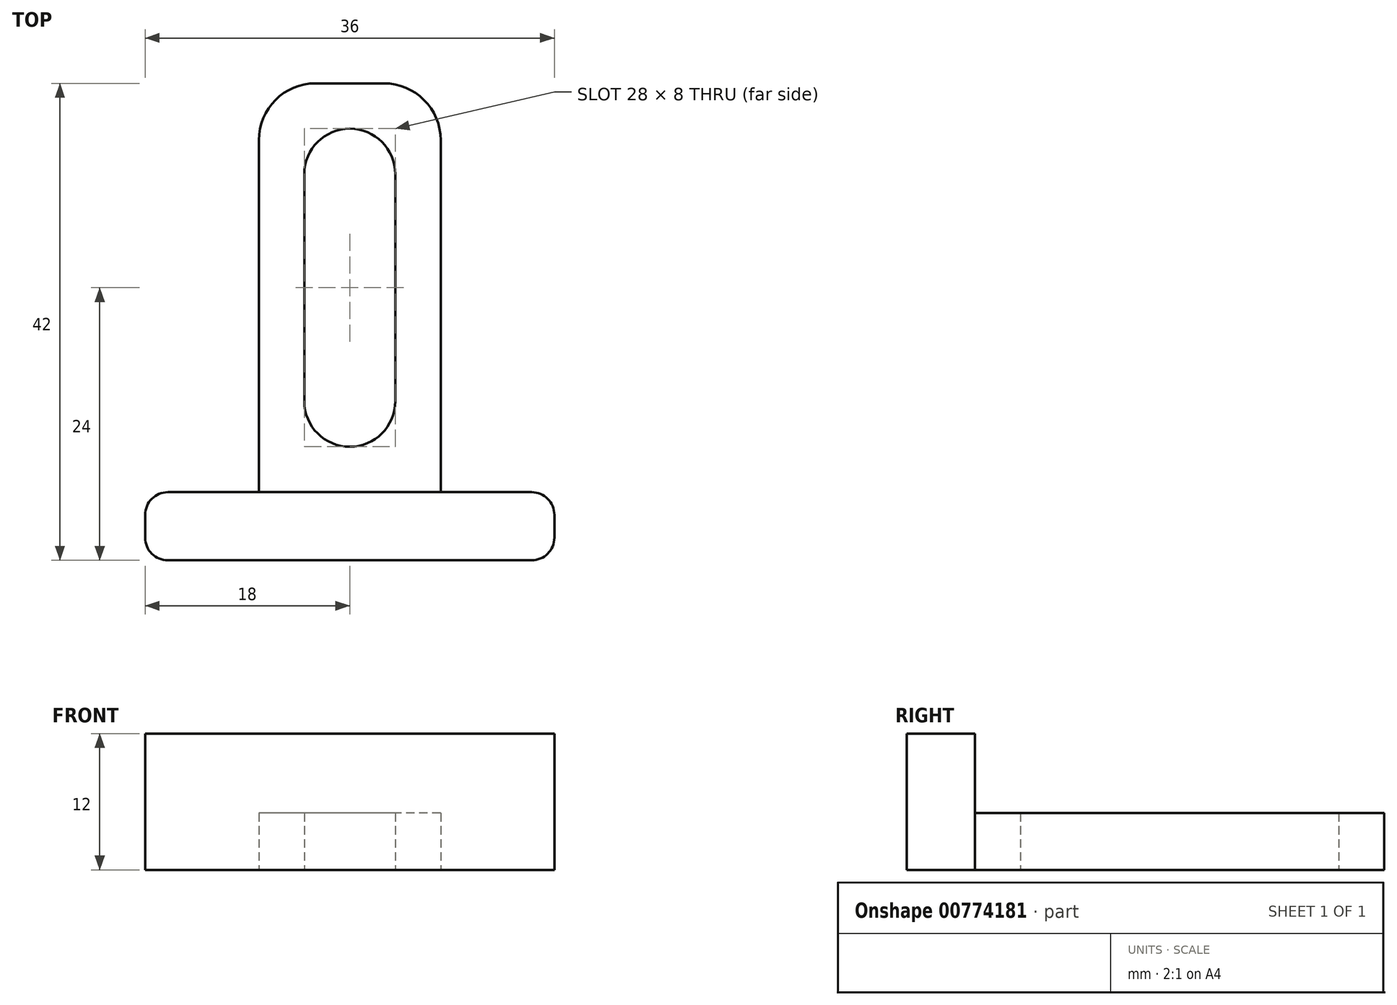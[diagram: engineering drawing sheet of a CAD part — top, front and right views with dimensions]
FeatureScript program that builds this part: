
annotation { "Feature Type Name" : "Feature", "Feature Type Description" : "" }
export const myFeature = defineFeature(function(context is Context, id is Id, definition is map)
    precondition{}
    {
        {
            var Q0;
            Q0=qCreatedBy(makeId("Top.planeOp"),FACE);
            var sketch = newSketch(context, id + "F0", { "sketchPlane" : qUnion([Q0])});
            skLineSegment(sketch, "E0", {"start": v(0, 0) * mm, "end": v(0, 20) * mm, "construction": true});
            skPoint(sketch, "E1.middle", {"position": v(0, 10) * mm});
            skLineSegment(sketch, "E2.bottom", {"start": v(8, -8) * mm, "end": v(-8, -8) * mm});
            skLineSegment(sketch, "E2.top", {"start": v(8, 28) * mm, "end": v(-8, 28) * mm});
            skLineSegment(sketch, "E2.left", {"start": v(8, -8) * mm, "end": v(8, 28) * mm});
            skLineSegment(sketch, "E2.right", {"start": v(-8, -8) * mm, "end": v(-8, 28) * mm});
            skLineSegment(sketch, "E3", {"start": v(4, 20) * mm, "end": v(4, 0) * mm});
            skLineSegment(sketch, "E4", {"start": v(-4, 0) * mm, "end": v(-4, 20) * mm});
            skArc(sketch, "E5", {"start": v(4, 20) * mm, "mid": v(0, 24) * mm, "end": v(-4, 20) * mm});
            skArc(sketch, "E6", {"start": v(4, 0) * mm, "mid": v(0, -4) * mm, "end": v(-4, 0) * mm});
            skSolve(sketch);
        }
        {
            var Q0;
            Q0 = qSketchRegion(id + "F0", true);
            extrude(context, id + "F1", {"entities" : qUnion([Q0]), "depth" : 5 * mm, "offsetDistance" : 25 * mm});
        }
        {
            var Q0;
            Q0=qCreatedBy(makeId("Top.planeOp"),FACE);
            var sketch = newSketch(context, id + "F2", { "sketchPlane" : qUnion([Q0])});
            skLineSegment(sketch, "E7", {"start": v(0, 0) * mm, "end": v(0, -8) * mm});
            skLineSegment(sketch, "E8", {"start": v(0, -8) * mm, "end": v(18, -8) * mm});
            skLineSegment(sketch, "E9", {"start": v(0, -8) * mm, "end": v(-18, -8) * mm});
            skLineSegment(sketch, "E10", {"start": v(-18, -8) * mm, "end": v(-18, -14) * mm});
            skLineSegment(sketch, "E11", {"start": v(18, -8) * mm, "end": v(18, -14) * mm});
            skLineSegment(sketch, "E12", {"start": v(18, -14) * mm, "end": v(-18, -14) * mm});
            skSolve(sketch);
        }
        {
            var Q0;
            Q0 = qSketchRegion(id + "F2", true);
            extrude(context, id + "F3", {"entities" : qUnion([Q0]), "operationType" : NewBodyOperationType.ADD, "depth" : 12 * mm, "offsetDistance" : 25 * mm});
        }
        {
            var Q0;
            Q0=makeQuery(id+"F3.opExtrude","SWEPT_EDGE",EDGE,{"disambiguationData":[OSD([sQuery(id+"F2.wireOp",EDGE,"E10"),sQuery(id+"F2.wireOp",EDGE,"E12")])]});
            var Q1;
            Q1=makeQuery(id+"F3.opExtrude","SWEPT_EDGE",EDGE,{"disambiguationData":[OSD([sQuery(id+"F2.wireOp",EDGE,"E9"),sQuery(id+"F2.wireOp",EDGE,"E10")])]});
            var Q2;
            Q2=makeQuery(id+"F3.opExtrude","SWEPT_EDGE",EDGE,{"disambiguationData":[OSD([sQuery(id+"F2.wireOp",EDGE,"E8"),sQuery(id+"F2.wireOp",EDGE,"E11")])]});
            var Q3;
            Q3=makeQuery(id+"F3.opExtrude","SWEPT_EDGE",EDGE,{"disambiguationData":[OSD([sQuery(id+"F2.wireOp",EDGE,"E11"),sQuery(id+"F2.wireOp",EDGE,"E12")])]});
            var Q4;
            Q4=makeQuery(id+"F1.opExtrude","CAP_EDGE",EDGE,{"disambiguationData":[OSD([sQuery(id+"F0.wireOp",EDGE,"E2.bottom")])],"isStart":false});
            var Q5;
            Q5=makeQuery(id+"F1.opExtrude","SWEPT_EDGE",EDGE,{"disambiguationData":[OSD([sQuery(id+"F0.wireOp",EDGE,"E2.bottom"),sQuery(id+"F0.wireOp",EDGE,"E2.left")])]});
            var Q6;
            Q6=makeQuery(id+"F1.opExtrude","SWEPT_EDGE",EDGE,{"disambiguationData":[OSD([sQuery(id+"F0.wireOp",EDGE,"E2.bottom"),sQuery(id+"F0.wireOp",EDGE,"E2.right")])]});
            fillet(context, id + "F4", {"entities" : qUnion([Q0, Q1, Q2, Q3, Q4, Q5, Q6]), "radius" : 2 * mm, "tangentPropagation" : true, "allowEdgeOverflow" : false});
        }
        {
            var Q0;
            Q0=makeQuery(id+"F1.opExtrude","SWEPT_EDGE",EDGE,{"disambiguationData":[OSD([sQuery(id+"F0.wireOp",EDGE,"E2.top"),sQuery(id+"F0.wireOp",EDGE,"E2.right")])]});
            var Q1;
            Q1=makeQuery(id+"F1.opExtrude","SWEPT_EDGE",EDGE,{"disambiguationData":[OSD([sQuery(id+"F0.wireOp",EDGE,"E2.top"),sQuery(id+"F0.wireOp",EDGE,"E2.left")])]});
            fillet(context, id + "F5", {"entities" : qUnion([Q0, Q1]), "radius" : 5 * mm, "tangentPropagation" : true, "allowEdgeOverflow" : false});
        }
    });
